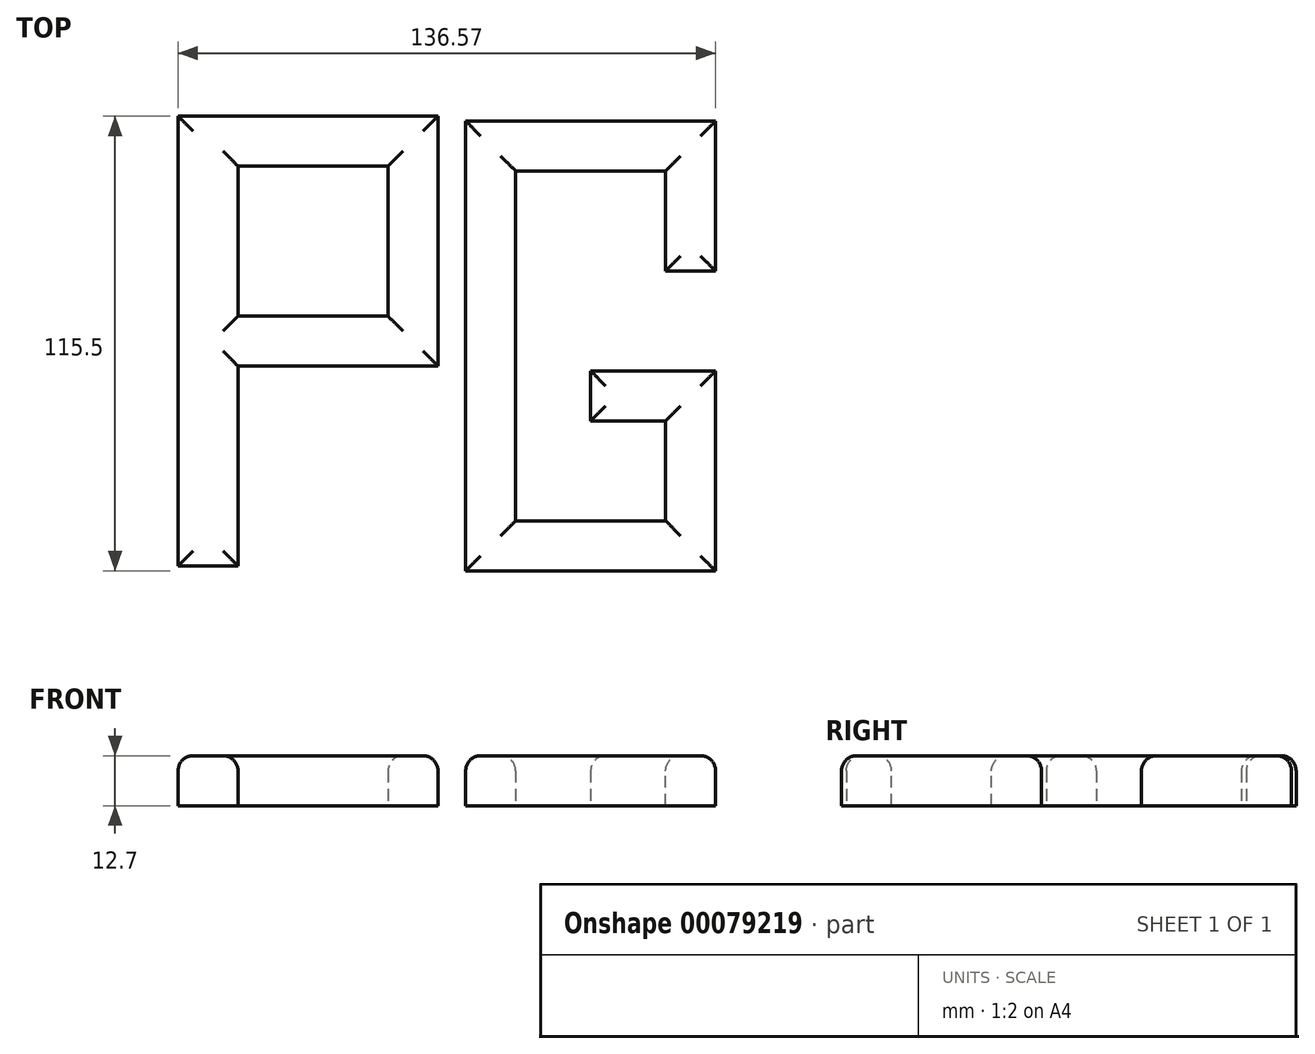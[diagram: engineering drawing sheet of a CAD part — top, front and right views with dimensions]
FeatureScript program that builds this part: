
annotation { "Feature Type Name" : "Feature", "Feature Type Description" : "" }
export const myFeature = defineFeature(function(context is Context, id is Id, definition is map)
    precondition{}
    {
        {
            var Q0;
            Q0=qCreatedBy(makeId("Top.planeOp"),FACE);
            var sketch = newSketch(context, id + "F0", { "sketchPlane" : qUnion([Q0])});
            skLineSegment(sketch, "E0.bottom", {"start": v(-68.8, 49.36) * mm, "end": v(-53.56, 49.36) * mm});
            skLineSegment(sketch, "E0.top", {"start": v(-68.8, -64.94) * mm, "end": v(-53.56, -64.94) * mm});
            skLineSegment(sketch, "E0.left", {"start": v(-68.8, 49.36) * mm, "end": v(-68.8, -64.94) * mm});
            skLineSegment(sketch, "E0.right", {"start": v(-53.56, 49.36) * mm, "end": v(-53.56, -64.94) * mm});
            skSolve(sketch);
        }
        {
            var Q0;
            Q0 = qSketchRegion(id + "F0", true);
            extrude(context, id + "F1", {"entities" : qUnion([Q0]), "depth" : 12.7 * mm});
        }
        {
            var Q0;
            Q0=makeQuery(id+"F1.opExtrude","SWEPT_FACE",FACE,{"disambiguationData":[OSD([sQuery(id+"F0.wireOp",EDGE,"E0.right")])]});
            var sketch = newSketch(context, id + "F2", { "sketchPlane" : qUnion([Q0])});
            skLineSegment(sketch, "E1.bottom", {"start": v(49.36, 12.7) * mm, "end": v(36.66, 12.7) * mm});
            skLineSegment(sketch, "E1.top", {"start": v(49.36, 0) * mm, "end": v(36.66, 0) * mm});
            skLineSegment(sketch, "E1.left", {"start": v(49.36, 12.7) * mm, "end": v(49.36, 0) * mm});
            skLineSegment(sketch, "E1.right", {"start": v(36.66, 12.7) * mm, "end": v(36.66, 0) * mm});
            skSolve(sketch);
        }
        {
            var Q0;
            Q0=makeQuery(id+"F2.imprint","IMPRINT",FACE,{"disambiguationData":[TD([[makeQuery(id+"F2.imprint","IMPRINT",EDGE,{"derivedFrom":sQuery(id+"F2.wireOp",EDGE,"E1.bottom")}),1.0]])]});
            extrude(context, id + "F3", {"entities" : qUnion([Q0]), "operationType" : NewBodyOperationType.ADD, "depth" : 50.8 * mm});
        }
        {
            var Q0;
            Q0=makeQuery(id+"F3.opExtrude","SWEPT_FACE",FACE,{"disambiguationData":[OSD([sQuery(id+"F2.wireOp",EDGE,"E1.right")])]});
            var sketch = newSketch(context, id + "F4", { "sketchPlane" : qUnion([Q0])});
            skLineSegment(sketch, "E2.bottom", {"start": v(-2.76, 12.7) * mm, "end": v(-15.46, 12.7) * mm});
            skLineSegment(sketch, "E2.top", {"start": v(-2.76, 0) * mm, "end": v(-15.46, 0) * mm});
            skLineSegment(sketch, "E2.left", {"start": v(-2.76, 12.7) * mm, "end": v(-2.76, 0) * mm});
            skLineSegment(sketch, "E2.right", {"start": v(-15.46, 12.7) * mm, "end": v(-15.46, 0) * mm});
            skSolve(sketch);
        }
        {
            var Q0;
            Q0=makeQuery(id+"F4.imprint","IMPRINT",FACE,{"disambiguationData":[TD([[makeQuery(id+"F4.imprint","IMPRINT",EDGE,{"derivedFrom":sQuery(id+"F4.wireOp",EDGE,"E2.bottom")}),1.0]])]});
            extrude(context, id + "F5", {"entities" : qUnion([Q0]), "operationType" : NewBodyOperationType.ADD, "depth" : 38.1 * mm});
        }
        {
            var Q0;
            Q0=makeQuery(id+"F1.opExtrude","SWEPT_FACE",FACE,{"disambiguationData":[OSD([sQuery(id+"F0.wireOp",EDGE,"E0.right")])]});
            var sketch = newSketch(context, id + "F6", { "sketchPlane" : qUnion([Q0])});
            skLineSegment(sketch, "E3.bottom", {"start": v(-14.14, 12.7) * mm, "end": v(-1.44, 12.7) * mm});
            skLineSegment(sketch, "E3.top", {"start": v(-14.14, 0) * mm, "end": v(-1.44, 0) * mm});
            skLineSegment(sketch, "E3.left", {"start": v(-14.14, 12.7) * mm, "end": v(-14.14, 0) * mm});
            skLineSegment(sketch, "E3.right", {"start": v(-1.44, 12.7) * mm, "end": v(-1.44, 0) * mm});
            skSolve(sketch);
        }
        {
            var Q0;
            Q0=makeQuery(id+"F6.imprint","IMPRINT",FACE,{"disambiguationData":[TD([[makeQuery(id+"F6.imprint","IMPRINT",EDGE,{"derivedFrom":sQuery(id+"F6.wireOp",EDGE,"E3.bottom")}),1.0]])]});
            extrude(context, id + "F7", {"entities" : qUnion([Q0]), "operationType" : NewBodyOperationType.ADD, "depth" : 50.8 * mm});
        }
        {
            var Q0;
            Q0=qCreatedBy(makeId("Top.planeOp"),FACE);
            var sketch = newSketch(context, id + "F8", { "sketchPlane" : qUnion([Q0])});
            skLineSegment(sketch, "E4.bottom", {"start": v(4.27, 48.16) * mm, "end": v(16.97, 48.16) * mm});
            skLineSegment(sketch, "E4.top", {"start": v(4.27, -66.14) * mm, "end": v(16.97, -66.14) * mm});
            skLineSegment(sketch, "E4.left", {"start": v(4.27, 48.16) * mm, "end": v(4.27, -66.14) * mm});
            skLineSegment(sketch, "E4.right", {"start": v(16.97, 48.16) * mm, "end": v(16.97, -66.14) * mm});
            skSolve(sketch);
        }
        {
            var Q0;
            Q0=makeQuery(id+"F8.imprint","IMPRINT",FACE,{"disambiguationData":[TD([[makeQuery(id+"F8.imprint","IMPRINT",EDGE,{"derivedFrom":sQuery(id+"F8.wireOp",EDGE,"E4.bottom")}),-1.0]])]});
            extrude(context, id + "F9", {"entities" : qUnion([Q0]), "depth" : 12.7 * mm});
        }
        {
            var Q0;
            Q0=makeQuery(id+"F9.opExtrude","SWEPT_FACE",FACE,{"disambiguationData":[OSD([sQuery(id+"F8.wireOp",EDGE,"E4.right")])]});
            var sketch = newSketch(context, id + "F10", { "sketchPlane" : qUnion([Q0])});
            skLineSegment(sketch, "E5.bottom", {"start": v(48.16, 12.7) * mm, "end": v(35.46, 12.7) * mm});
            skLineSegment(sketch, "E5.top", {"start": v(48.16, 0) * mm, "end": v(35.46, 0) * mm});
            skLineSegment(sketch, "E5.left", {"start": v(48.16, 12.7) * mm, "end": v(48.16, 0) * mm});
            skLineSegment(sketch, "E5.right", {"start": v(35.46, 12.7) * mm, "end": v(35.46, 0) * mm});
            skSolve(sketch);
        }
        {
            var Q0;
            Q0=makeQuery(id+"F10.imprint","IMPRINT",FACE,{"disambiguationData":[TD([[makeQuery(id+"F10.imprint","IMPRINT",EDGE,{"derivedFrom":sQuery(id+"F10.wireOp",EDGE,"E5.bottom")}),1.0]])]});
            extrude(context, id + "F11", {"entities" : qUnion([Q0]), "operationType" : NewBodyOperationType.ADD, "depth" : 50.8 * mm});
        }
        {
            var Q0;
            Q0=makeQuery(id+"F11.opExtrude","SWEPT_FACE",FACE,{"disambiguationData":[OSD([sQuery(id+"F10.wireOp",EDGE,"E5.right")])]});
            var sketch = newSketch(context, id + "F12", { "sketchPlane" : qUnion([Q0])});
            skLineSegment(sketch, "E6.bottom", {"start": v(67.77, 0) * mm, "end": v(55.07, 0) * mm});
            skLineSegment(sketch, "E6.top", {"start": v(67.77, 12.7) * mm, "end": v(55.07, 12.7) * mm});
            skLineSegment(sketch, "E6.left", {"start": v(67.77, 0) * mm, "end": v(67.77, 12.7) * mm});
            skLineSegment(sketch, "E6.right", {"start": v(55.07, 0) * mm, "end": v(55.07, 12.7) * mm});
            skSolve(sketch);
        }
        {
            var Q0;
            Q0=makeQuery(id+"F12.imprint","IMPRINT",FACE,{"disambiguationData":[TD([[makeQuery(id+"F12.imprint","IMPRINT",EDGE,{"derivedFrom":sQuery(id+"F12.wireOp",EDGE,"E6.bottom")}),-1.0]])]});
            extrude(context, id + "F13", {"entities" : qUnion([Q0]), "operationType" : NewBodyOperationType.ADD, "depth" : 25.4 * mm});
        }
        {
            var Q0;
            Q0=makeQuery(id+"F9.opExtrude","SWEPT_FACE",FACE,{"disambiguationData":[OSD([sQuery(id+"F8.wireOp",EDGE,"E4.right")])]});
            var sketch = newSketch(context, id + "F14", { "sketchPlane" : qUnion([Q0])});
            skLineSegment(sketch, "E7.bottom", {"start": v(-66.14, 0) * mm, "end": v(-53.44, 0) * mm});
            skLineSegment(sketch, "E7.top", {"start": v(-66.14, 12.7) * mm, "end": v(-53.44, 12.7) * mm});
            skLineSegment(sketch, "E7.left", {"start": v(-66.14, 0) * mm, "end": v(-66.14, 12.7) * mm});
            skLineSegment(sketch, "E7.right", {"start": v(-53.44, 0) * mm, "end": v(-53.44, 12.7) * mm});
            skSolve(sketch);
        }
        {
            var Q0;
            Q0=makeQuery(id+"F14.imprint","IMPRINT",FACE,{"disambiguationData":[TD([[makeQuery(id+"F14.imprint","IMPRINT",EDGE,{"derivedFrom":sQuery(id+"F14.wireOp",EDGE,"E7.bottom")}),-1.0]])]});
            extrude(context, id + "F15", {"entities" : qUnion([Q0]), "operationType" : NewBodyOperationType.ADD, "depth" : 50.8 * mm});
        }
        {
            var Q0;
            Q0=makeQuery(id+"F15.opExtrude","SWEPT_FACE",FACE,{"disambiguationData":[OSD([sQuery(id+"F14.wireOp",EDGE,"E7.right")])]});
            var sketch = newSketch(context, id + "F16", { "sketchPlane" : qUnion([Q0])});
            skLineSegment(sketch, "E8.bottom", {"start": v(-67.77, 12.7) * mm, "end": v(-55.07, 12.7) * mm});
            skLineSegment(sketch, "E8.top", {"start": v(-67.77, 0) * mm, "end": v(-55.07, 0) * mm});
            skLineSegment(sketch, "E8.left", {"start": v(-67.77, 12.7) * mm, "end": v(-67.77, 0) * mm});
            skLineSegment(sketch, "E8.right", {"start": v(-55.07, 12.7) * mm, "end": v(-55.07, 0) * mm});
            skSolve(sketch);
        }
        {
            var Q0;
            Q0=makeQuery(id+"F16.imprint","IMPRINT",FACE,{"disambiguationData":[TD([[makeQuery(id+"F16.imprint","IMPRINT",EDGE,{"derivedFrom":sQuery(id+"F16.wireOp",EDGE,"E8.bottom")}),-1.0]])]});
            extrude(context, id + "F17", {"entities" : qUnion([Q0]), "operationType" : NewBodyOperationType.ADD, "depth" : 38.1 * mm});
        }
        {
            var Q0;
            Q0=makeQuery(id+"F17.opExtrude","SWEPT_FACE",FACE,{"disambiguationData":[OSD([sQuery(id+"F16.wireOp",EDGE,"E8.right")])]});
            var sketch = newSketch(context, id + "F18", { "sketchPlane" : qUnion([Q0])});
            skLineSegment(sketch, "E9.bottom", {"start": v(15.34, 0) * mm, "end": v(28.04, 0) * mm});
            skLineSegment(sketch, "E9.top", {"start": v(15.34, 12.7) * mm, "end": v(28.04, 12.7) * mm});
            skLineSegment(sketch, "E9.left", {"start": v(15.34, 0) * mm, "end": v(15.34, 12.7) * mm});
            skLineSegment(sketch, "E9.right", {"start": v(28.04, 0) * mm, "end": v(28.04, 12.7) * mm});
            skSolve(sketch);
        }
        {
            var Q0;
            Q0=makeQuery(id+"F18.imprint","IMPRINT",FACE,{"disambiguationData":[TD([[makeQuery(id+"F18.imprint","IMPRINT",EDGE,{"derivedFrom":sQuery(id+"F18.wireOp",EDGE,"E9.bottom")}),1.0]])]});
            extrude(context, id + "F19", {"entities" : qUnion([Q0]), "operationType" : NewBodyOperationType.ADD, "depth" : 19.05 * mm});
        }
        {
            var Q0;
            Q0=makeQuery(id+"F7.boolean.opBoolean","MERGE",FACE,{"derivedFrom":[makeQuery(id+"F5.boolean.opBoolean","MERGE",FACE,{"derivedFrom":[makeQuery(id+"F3.boolean.opBoolean","MERGE",FACE,{"derivedFrom":[makeQuery(id+"F1.opExtrude","CAP_FACE",FACE,{"disambiguationData":[OSD([sQuery(id+"F0.wireOp",EDGE,"E0.bottom"),sQuery(id+"F0.wireOp",EDGE,"E0.top"),sQuery(id+"F0.wireOp",EDGE,"E0.left"),sQuery(id+"F0.wireOp",EDGE,"E0.right")])],"isStart":false}),makeQuery(id+"F3.opExtrude","SWEPT_FACE",FACE,{"disambiguationData":[OSD([sQuery(id+"F2.wireOp",EDGE,"E1.bottom")])]})]}),makeQuery(id+"F5.opExtrude","SWEPT_FACE",FACE,{"disambiguationData":[OSD([sQuery(id+"F4.wireOp",EDGE,"E2.bottom")])]})]}),makeQuery(id+"F7.opExtrude","SWEPT_FACE",FACE,{"disambiguationData":[OSD([sQuery(id+"F6.wireOp",EDGE,"E3.bottom")])]})]});
            var Q1;
            Q1=makeQuery(id+"F19.boolean.opBoolean","MERGE",FACE,{"derivedFrom":[makeQuery(id+"F17.boolean.opBoolean","MERGE",FACE,{"derivedFrom":[makeQuery(id+"F15.boolean.opBoolean","MERGE",FACE,{"derivedFrom":[makeQuery(id+"F13.boolean.opBoolean","MERGE",FACE,{"derivedFrom":[makeQuery(id+"F11.boolean.opBoolean","MERGE",FACE,{"derivedFrom":[makeQuery(id+"F9.opExtrude","CAP_FACE",FACE,{"disambiguationData":[OSD([sQuery(id+"F8.wireOp",EDGE,"E4.bottom"),sQuery(id+"F8.wireOp",EDGE,"E4.top"),sQuery(id+"F8.wireOp",EDGE,"E4.left"),sQuery(id+"F8.wireOp",EDGE,"E4.right")])],"isStart":false}),makeQuery(id+"F11.opExtrude","SWEPT_FACE",FACE,{"disambiguationData":[OSD([sQuery(id+"F10.wireOp",EDGE,"E5.bottom")])]})]}),makeQuery(id+"F13.opExtrude","SWEPT_FACE",FACE,{"disambiguationData":[OSD([sQuery(id+"F12.wireOp",EDGE,"E6.top")])]})]}),makeQuery(id+"F15.opExtrude","SWEPT_FACE",FACE,{"disambiguationData":[OSD([sQuery(id+"F14.wireOp",EDGE,"E7.top")])]})]}),makeQuery(id+"F17.opExtrude","SWEPT_FACE",FACE,{"disambiguationData":[OSD([sQuery(id+"F16.wireOp",EDGE,"E8.bottom")])]})]}),makeQuery(id+"F19.opExtrude","SWEPT_FACE",FACE,{"disambiguationData":[OSD([sQuery(id+"F18.wireOp",EDGE,"E9.top")])]})]});
            fillet(context, id + "F20", {"entities" : qUnion([Q0, Q1]), "radius" : 3.8 * mm, "tangentPropagation" : true, "allowEdgeOverflow" : false});
        }
    });
